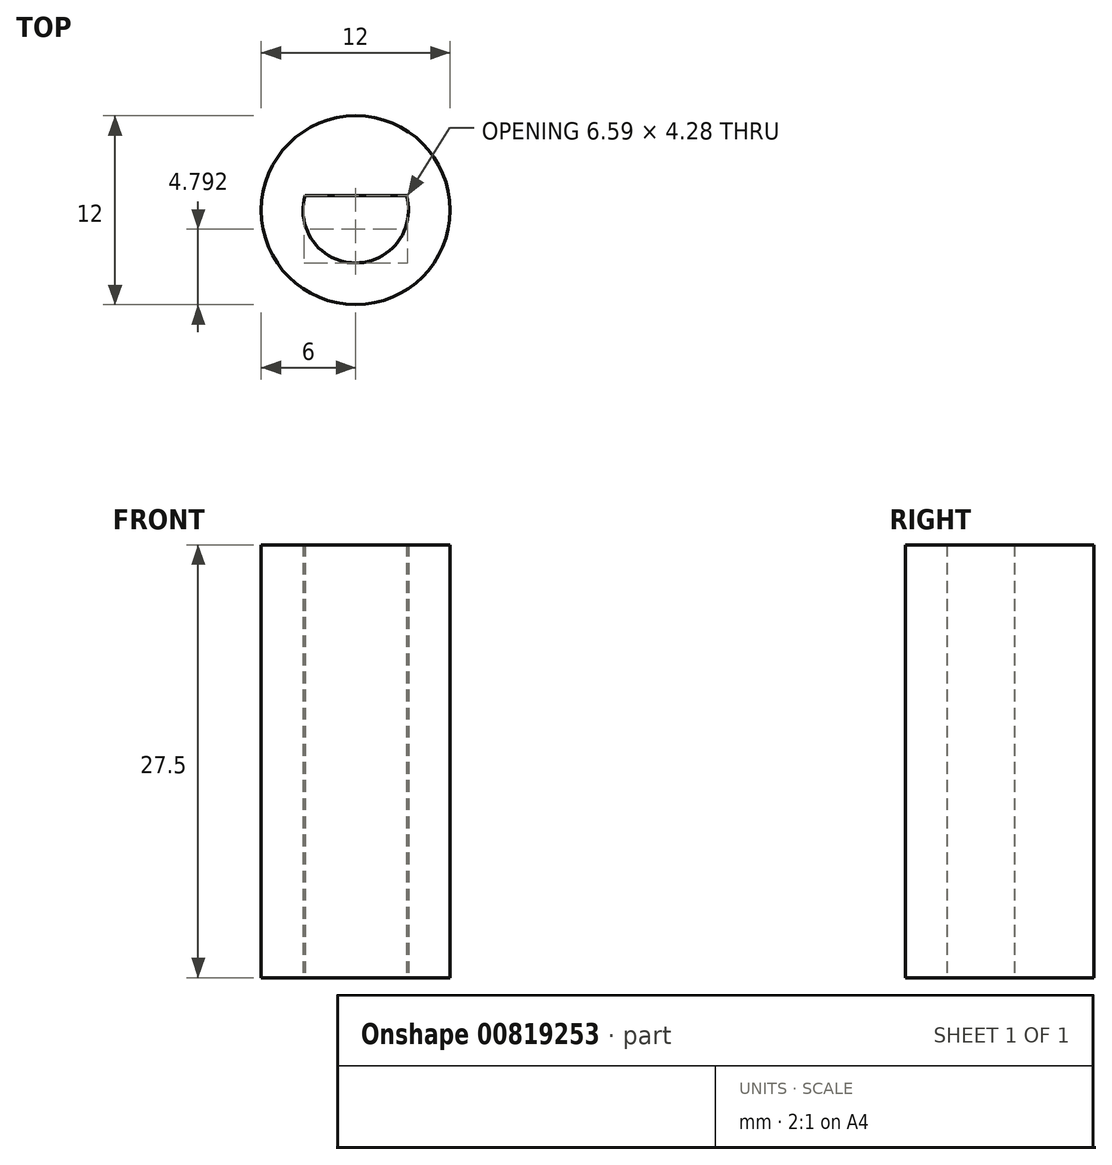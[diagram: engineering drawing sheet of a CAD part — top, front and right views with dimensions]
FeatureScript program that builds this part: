
annotation { "Feature Type Name" : "Feature", "Feature Type Description" : "" }
export const myFeature = defineFeature(function(context is Context, id is Id, definition is map)
    precondition{}
    {
        {
            var Q0;
            Q0=qCreatedBy(makeId("Top.planeOp"),FACE);
            var sketch = newSketch(context, id + "F0", { "sketchPlane" : qUnion([Q0])});
            skCircle(sketch, "E0", {"center": v(0, 0) * mm, "radius": 6 * mm});
            skArc(sketch, "E1", {"start": v(-2.58, 2.13) * mm, "mid": v(0, -3.35) * mm, "end": v(2.58, 2.13) * mm});
            skArc(sketch, "E2", {"start": v(2.58, 2.13) * mm, "mid": v(0, 3.35) * mm, "end": v(-2.58, 2.13) * mm});
            skLineSegment(sketch, "E3", {"start": v(0, 0.93) * mm, "end": v(-3.22, 0.93) * mm});
            skLineSegment(sketch, "E4", {"start": v(0, 0.93) * mm, "end": v(3.22, 0.93) * mm});
            skPoint(sketch, "E5.end.orphan", {"position": v(0, -3.35) * mm});
            skSolve(sketch);
        }
        {
            var Q0;
            Q0=qSketchRegion(id+"F0",true);
            var Q1;
            {var subQ1=sQuery(id+"F0.wireOp",EDGE,"E2");Q1=makeQuery(id+"F0.imprint","IMPRINT",FACE,{"disambiguationData":[TD([[makeQuery(id+"F0.imprint","IMPRINT",EDGE,{"derivedFrom":subQ1}),1.0]])]});}
            extrude(context, id + "F1", {"entities" : qUnion([Q0, Q1]), "depth" : 27.5 * mm, "offsetDistance" : 25.4 * mm});
        }
    });
